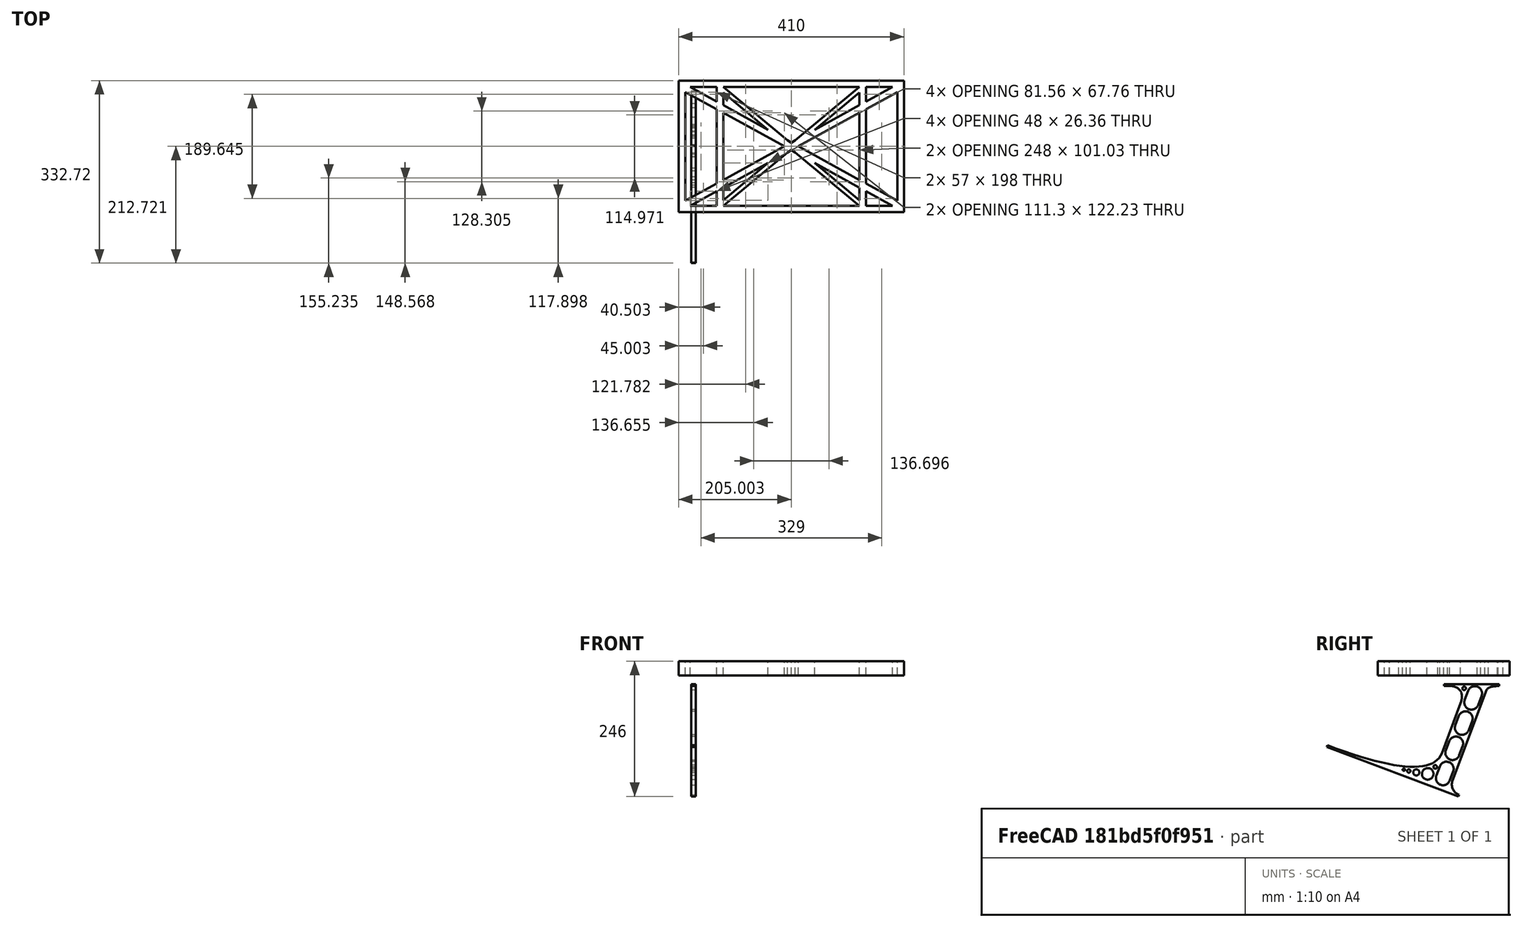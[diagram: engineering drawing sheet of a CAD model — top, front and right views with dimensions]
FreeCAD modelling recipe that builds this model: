
FCSTD DOCUMENT  (FreeCAD 0.19R0.19.2)
Label: laptopStand039
License: All rights reserved
LicenseURL: http://en.wikipedia.org/wiki/All_rights_reserved
objects: Sketcher::SketchObject×3, Part::Extrusion×2
note: 5 computed .brp shape members not serialized (recipe doc carries the construction recipe); baked Part::Feature solids carry a one-line shape summary decoded from their .brp

FEATURE [Sketcher::SketchObject] Sketch
  FullyConstrained = true
  sketch-geometry (52):
    g0: LineSegment StartX=-22.9272 StartY=136.221 StartZ=0 EndX=-22.9272 EndY=-103.779 EndZ=0
    g1: LineSegment StartX=-22.9272 StartY=136.221 StartZ=0 EndX=387.073 EndY=136.221 EndZ=0
    g2: LineSegment StartX=-22.9272 StartY=-103.779 StartZ=0 EndX=387.073 EndY=-103.779 EndZ=0
    g3: LineSegment StartX=387.073 StartY=136.221 StartZ=0 EndX=387.073 EndY=-103.779 EndZ=0
    g4: LineSegment StartX=375.073 StartY=115.221 StartZ=0 EndX=318.073 EndY=83.9235 EndZ=0
    g5: LineSegment StartX=-10.9272 StartY=-82.7794 StartZ=0 EndX=46.0728 EndY=-51.4823 EndZ=0
    g6: LineSegment StartX=-1.92719 StartY=124.221 StartZ=0 EndX=46.0728 EndY=97.8651 EndZ=0
    g7: LineSegment StartX=366.073 StartY=-91.7794 StartZ=0 EndX=318.073 EndY=-65.424 EndZ=0
    g8: LineSegment StartX=-10.9272 StartY=115.221 StartZ=0 EndX=-10.9272 EndY=-82.7794 EndZ=0
    g9: LineSegment StartX=375.073 StartY=-82.7794 StartZ=0 EndX=375.073 EndY=115.221 EndZ=0
    g10: LineSegment StartX=-1.92719 StartY=-91.7794 StartZ=0 EndX=46.0728 EndY=-91.7794 EndZ=0
    g11: LineSegment StartX=318.073 StartY=124.221 StartZ=0 EndX=366.073 EndY=124.221 EndZ=0
    g12: LineSegment StartX=306.073 StartY=-81.8102 StartZ=0 EndX=224.513 EndY=-14.0532 EndZ=0
    g13: LineSegment StartX=58.0728 StartY=114.251 StartZ=0 EndX=139.632 EndY=46.4944 EndZ=0
    g14: LineSegment StartX=306.073 StartY=124.221 StartZ=0 EndX=189.124 EndY=27.0628 EndZ=0
    g15: LineSegment StartX=58.0728 StartY=-91.7794 StartZ=0 EndX=175.022 EndY=5.37834 EndZ=0
    g16: LineSegment StartX=46.0728 StartY=124.221 StartZ=0 EndX=46.0728 EndY=97.8651 EndZ=0
    g17: LineSegment StartX=58.0728 StartY=-81.8102 StartZ=0 EndX=58.0728 EndY=-58.8351 EndZ=0
    g18: LineSegment StartX=318.073 StartY=124.221 StartZ=0 EndX=318.073 EndY=97.8651 EndZ=0
    g19: LineSegment StartX=306.073 StartY=114.251 StartZ=0 EndX=306.073 EndY=91.2763 EndZ=0
    g20: LineSegment StartX=182.073 StartY=23.1914 StartZ=0 EndX=189.124 EndY=27.0628 EndZ=0
    g21: LineSegment StartX=182.073 StartY=9.24976 StartZ=0 EndX=175.022 EndY=5.37834 EndZ=0
    g22: LineSegment StartX=224.513 StartY=46.4944 StartZ=0 EndX=306.073 EndY=114.251 EndZ=0
    g23: LineSegment StartX=175.022 StartY=27.0628 StartZ=0 EndX=58.0728 EndY=124.221 EndZ=0
    g24: LineSegment StartX=169.377 StartY=16.2206 StartZ=0 EndX=58.0728 EndY=77.3346 EndZ=0
    g25: LineSegment StartX=139.632 StartY=-14.0532 StartZ=0 EndX=58.0728 EndY=-81.8102 EndZ=0
    g26: LineSegment StartX=194.768 StartY=16.2206 StartZ=0 EndX=306.073 EndY=-44.8935 EndZ=0
    g27: LineSegment StartX=224.513 StartY=46.4944 StartZ=0 EndX=306.073 EndY=91.2763 EndZ=0
    g28: LineSegment StartX=175.022 StartY=27.0628 StartZ=0 EndX=182.073 EndY=23.1914 EndZ=0
    g29: LineSegment StartX=139.632 StartY=-14.0532 StartZ=0 EndX=58.0728 EndY=-58.8351 EndZ=0
    g30: LineSegment StartX=189.124 StartY=5.37834 StartZ=0 EndX=182.073 EndY=9.24976 EndZ=0
    g31: LineSegment StartX=189.124 StartY=5.37834 StartZ=0 EndX=306.073 EndY=-91.7794 EndZ=0
    g32: LineSegment StartX=306.073 StartY=77.3346 StartZ=0 EndX=306.073 EndY=-44.8935 EndZ=0
    g33: LineSegment StartX=318.073 StartY=83.9235 StartZ=0 EndX=318.073 EndY=-51.4823 EndZ=0
    g34: LineSegment StartX=318.073 StartY=97.8651 StartZ=0 EndX=366.073 EndY=124.221 EndZ=0
    g35: LineSegment StartX=306.073 StartY=77.3346 StartZ=0 EndX=194.768 EndY=16.2206 EndZ=0
    g36: LineSegment StartX=306.073 StartY=-58.8351 StartZ=0 EndX=224.513 EndY=-14.0532 EndZ=0
    g37: LineSegment StartX=306.073 StartY=-58.8351 StartZ=0 EndX=306.073 EndY=-81.8102 EndZ=0
    g38: LineSegment StartX=318.073 StartY=-51.4823 StartZ=0 EndX=375.073 EndY=-82.7794 EndZ=0
    g39: LineSegment StartX=318.073 StartY=-65.424 StartZ=0 EndX=318.073 EndY=-91.7794 EndZ=0
    g40: LineSegment StartX=306.073 StartY=124.221 StartZ=0 EndX=58.0728 EndY=124.221 EndZ=0
    g41: LineSegment StartX=318.073 StartY=-91.7794 StartZ=0 EndX=366.073 EndY=-91.7794 EndZ=0
    g42: LineSegment StartX=58.0728 StartY=-91.7794 StartZ=0 EndX=306.073 EndY=-91.7794 EndZ=0
    g43: LineSegment StartX=58.0728 StartY=-44.8935 StartZ=0 EndX=58.0728 EndY=77.3346 EndZ=0
    g44: LineSegment StartX=46.0728 StartY=-65.424 StartZ=0 EndX=-1.92719 EndY=-91.7794 EndZ=0
    g45: LineSegment StartX=46.0728 StartY=-65.424 StartZ=0 EndX=46.0728 EndY=-91.7794 EndZ=0
    g46: LineSegment StartX=58.0728 StartY=-44.8935 StartZ=0 EndX=169.377 EndY=16.2206 EndZ=0
    g47: LineSegment StartX=58.0728 StartY=91.2763 StartZ=0 EndX=58.0728 EndY=114.251 EndZ=0
    g48: LineSegment StartX=46.0728 StartY=83.9235 StartZ=0 EndX=46.0728 EndY=-51.4823 EndZ=0
    g49: LineSegment StartX=46.0728 StartY=124.221 StartZ=0 EndX=-1.92719 EndY=124.221 EndZ=0
    g50: LineSegment StartX=58.0728 StartY=91.2763 StartZ=0 EndX=139.632 EndY=46.4944 EndZ=0
    g51: LineSegment StartX=46.0728 StartY=83.9235 StartZ=0 EndX=-10.9272 EndY=115.221 EndZ=0
  constraints (102):
    c: Vertical(g0)
    c: Distance(g0) = 240
    c: Horizontal(g1)
    c: Distance(g1) = 410
    c: Coincident(g1,g0)
    c: Coincident(g2,g0)
    c: Horizontal(g2)
    c: Coincident(g3,g1)
    c: Vertical(g3)
    c: Coincident(g2,g3)
    c: Block(g1)
    c: Horizontal(g10)
    c: Horizontal(g11)
    c: PointOnObject(g35,g6)
    c: Coincident(g28,g20)
    c: Coincident(g30,g21)
    c: Tangent(g7,g24)
    c: PointOnObject(g24,g5)
    c: PointOnObject(g26,g4)
    c: Coincident(g20,g14)
    c: Tangent(g20,g27)
    c: Coincident(g50,g13)
    c: Coincident(g28,g23)
    c: Coincident(g22,g27)
    c: Coincident(g21,g15)
    c: Coincident(g29,g25)
    c: Tangent(g21,g29)
    c: Coincident(g36,g12)
    c: Coincident(g31,g30)
    c: Coincident(g22,g19)
    c: Tangent(g19,g32)
    c: Tangent(g18,g33)
    c: Coincident(g27,g19)
    c: Tangent(g27,g34)
    c: Coincident(g4,g33)
    c: Coincident(g35,g32)
    c: Tangent(g4,g35)
    c: Coincident(g37,g12)
    c: Tangent(g7,g36)
    c: Tangent(g32,g37)
    c: Coincident(g26,g32)
    c: Tangent(g26,g38)
    c: Coincident(g33,g38)
    c: Coincident(g39,g7)
    c: Tangent(g33,g39)
    c: Coincident(g25,g17)
    c: Tangent(g17,g43)
    c: Coincident(g29,g17)
    c: Tangent(g29,g44)
    c: Coincident(g45,g44)
    c: Tangent(g16,g45)
    c: Coincident(g5,g48)
    c: Coincident(g46,g43)
    c: Tangent(g5,g46)
    c: Tangent(g43,g47)
    c: Tangent(g16,g48)
    c: Coincident(g13,g47)
    c: PointOnObject(g40,g23)
    c: Tangent(g40,g49)
    c: Coincident(g6,g16)
    c: Coincident(g50,g47)
    c: Tangent(g6,g50)
    c: Coincident(g24,g43)
    c: Coincident(g51,g48)
    c: Tangent(g24,g51)
    c: Block(g23)
    c: Block(g14)
    c: Block(g20)
    c: Block(g40)
    c: Block(g18)
    c: Block(g34)
    c: Block(g4)
    c: Block(g38)
    c: Block(g9)
    c: Block(g36)
    c: Block(g37)
    c: Block(g7)
    c: Block(g39)
    c: Block(g22)
    c: Block(g31)
    c: Block(g42)
    c: Block(g21)
    c: Block(g15)
    c: Block(g29)
    c: Block(g25)
    c: Block(g45)
    c: Block(g44)
    c: Block(g5)
    c: Block(g8)
    c: Block(g51)
    c: Block(g6)
    c: Block(g16)
    c: Block(g13)
    c: Block(g47)
    c: Block(g35)
    c: Block(g32)
    c: Block(g24)
    c: Block(g46)
    c: Block(g49)
    c: Block(g11)
    c: Block(g41)
    c: Block(g10)
FEATURE [Part::Extrusion] Extrude
  Base = -> Sketch
  Dir = (0,0,1)
  DirMode = 2
  FaceMakerClass = Part::FaceMakerBullseye
  LengthFwd = 26
  LengthRev = 0
  Solid = true
  Symmetric = false
FEATURE [Sketcher::SketchObject] Sketch001
  FullyConstrained = true
  MapMode = 4
  Placement = pos=(0,0,0) rot=(0.57735,0.57735,0.57735;2.0944rad)
  Support = -> [Sketch]
  sketch-geometry (46):
    g0: BSplineCurve PolesCount=3 KnotsCount=2 Degree=2 IsPeriodic=0
    g1: ArcOfCircle CenterX=73.122 CenterY=-32.2909 CenterZ=0 NormalX=0 NormalY=0 NormalZ=1 AngleXU=0 Radius=13 StartAngle=5.92268 EndAngle=9.06428
    g2: ArcOfCircle CenterX=66.7816 CenterY=-49.1439 CenterZ=0 NormalX=0 NormalY=0 NormalZ=1 AngleXU=0 Radius=13 StartAngle=2.78068 EndAngle=5.92131
    g3: ArcOfCircle CenterX=55.9263 CenterY=-78.1807 CenterZ=0 NormalX=0 NormalY=0 NormalZ=1 AngleXU=0 Radius=13 StartAngle=5.92268 EndAngle=9.06428
    g4: ArcOfCircle CenterX=49.5884 CenterY=-95.0342 CenterZ=0 NormalX=0 NormalY=0 NormalZ=1 AngleXU=0 Radius=13 StartAngle=2.78068 EndAngle=5.92131
    g5: ArcOfCircle CenterX=38.7206 CenterY=-124.067 CenterZ=0 NormalX=0 NormalY=0 NormalZ=1 AngleXU=0 Radius=13 StartAngle=5.92268 EndAngle=9.06428
    g6: ArcOfCircle CenterX=32.3875 CenterY=-140.92 CenterZ=0 NormalX=0 NormalY=0 NormalZ=1 AngleXU=0 Radius=13 StartAngle=2.78068 EndAngle=5.92131
    g7: ArcOfCircle CenterX=21.4715 CenterY=-169.934 CenterZ=0 NormalX=0 NormalY=0 NormalZ=1 AngleXU=0 Radius=13 StartAngle=5.92268 EndAngle=9.06428
    g8: ArcOfCircle CenterX=15.1336 CenterY=-186.787 CenterZ=0 NormalX=0 NormalY=0 NormalZ=1 AngleXU=0 Radius=13 StartAngle=2.78068 EndAngle=5.92131
    g9-g12: Circle x4 (B-spline internal-alignment scaffolding for g13; pole/knot coordinates omitted)
    g13: BSplineCurve PolesCount=4 KnotsCount=2 Degree=3 IsPeriodic=0
    g14: GeomPoint X=28.8094 Y=-19.0875 Z=0
    g15: GeomPoint X=47.0443 Y=-50.4712 Z=0
    g16: Circle CenterX=53.5586 CenterY=-23.2695 CenterZ=0 NormalX=0 NormalY=0 NormalZ=1 AngleXU=0 Radius=3.24518
    g17: Circle CenterX=-195.441 CenterY=-127.082 CenterZ=0 NormalX=0 NormalY=0 NormalZ=1 AngleXU=0 Radius=1
    g18: Circle CenterX=-8.24091 CenterY=-197.481 CenterZ=0 NormalX=0 NormalY=0 NormalZ=1 AngleXU=0 Radius=1
    g19: Circle CenterX=12.8789 CenterY=-141.321 CenterZ=0 NormalX=0 NormalY=0 NormalZ=1 AngleXU=0 Radius=1
    g20: BSplineCurve PolesCount=3 KnotsCount=2 Degree=2 IsPeriodic=0
    g21: GeomPoint X=-195.441 Y=-127.082 Z=0
    g22: GeomPoint X=12.8789 Y=-141.321 Z=0
    g23: Circle CenterX=-12.8016 CenterY=-179.036 CenterZ=0 NormalX=0 NormalY=0 NormalZ=1 AngleXU=0 Radius=10.5072
    g24: Circle CenterX=0.933922 CenterY=-166.43 CenterZ=0 NormalX=0 NormalY=0 NormalZ=1 AngleXU=0 Radius=3.26661
    g25: Circle CenterX=-33.5518 CenterY=-176.44 CenterZ=0 NormalX=0 NormalY=0 NormalZ=1 AngleXU=0 Radius=5.64388
    g26: Circle CenterX=-47.2366 CenterY=-173.859 CenterZ=0 NormalX=0 NormalY=0 NormalZ=1 AngleXU=0 Radius=3.01653
    g27: Circle CenterX=-56.2595 CenterY=-171.456 CenterZ=0 NormalX=0 NormalY=0 NormalZ=1 AngleXU=0 Radius=2.12826
    g28: ArcOfCircle CenterX=51.2151 CenterY=-198.473 CenterZ=0 NormalX=0 NormalY=0 NormalZ=1 AngleXU=0 Radius=20 StartAngle=2.78189 EndAngle=4.35269
    g29: LineSegment StartX=32.4951 StartY=-191.433 StartZ=0 EndX=94.6577 EndY=-26.1351 EndZ=0
    g30: LineSegment StartX=43.1192 StartY=-220.001 StartZ=0 EndX=-196.497 EndY=-129.89 EndZ=0
    g31: LineSegment StartX=43.1192 StartY=-220.001 StartZ=0 EndX=44.1752 EndY=-217.193 EndZ=0
    g32: LineSegment StartX=117.223 StartY=-19.0875 StartZ=0 EndX=117.223 EndY=-16.0875 EndZ=0
    g33: LineSegment StartX=117.223 StartY=-16.0875 StartZ=0 EndX=17.2232 EndY=-16.0875 EndZ=0
    g34: LineSegment StartX=17.2232 StartY=-16.0875 StartZ=0 EndX=17.2232 EndY=-19.0875 EndZ=0
    g35: LineSegment StartX=28.8094 StartY=-19.0875 StartZ=0 EndX=17.2232 EndY=-19.0875 EndZ=0
    g36: LineSegment StartX=47.0443 StartY=-50.4712 StartZ=0 EndX=12.8789 EndY=-141.321 EndZ=0
    g37: LineSegment StartX=-195.441 StartY=-127.082 StartZ=0 EndX=-196.497 EndY=-129.89 EndZ=0
    g38: LineSegment StartX=85.2864 StartY=-36.8765 StartZ=0 EndX=78.9396 EndY=-53.7463 EndZ=0
    g39: LineSegment StartX=60.9577 StartY=-27.7052 StartZ=0 EndX=54.6191 EndY=-44.5532 EndZ=0
    g40: LineSegment StartX=68.0907 StartY=-82.7664 StartZ=0 EndX=61.7465 EndY=-99.6365 EndZ=0
    g41: LineSegment StartX=43.7619 StartY=-73.595 StartZ=0 EndX=37.426 EndY=-90.4435 EndZ=0
    g42: LineSegment StartX=50.885 StartY=-128.652 StartZ=0 EndX=44.5456 EndY=-145.522 EndZ=0
    g43: LineSegment StartX=26.5562 StartY=-119.481 StartZ=0 EndX=20.2251 EndY=-136.329 EndZ=0
    g44: LineSegment StartX=9.3071 StartY=-165.349 StartZ=0 EndX=2.97115 EndY=-182.197 EndZ=0
    g45: LineSegment StartX=33.6358 StartY=-174.52 StartZ=0 EndX=27.2917 EndY=-191.39 EndZ=0
  constraints (70):
    c: Block(g0)
    c: Block(g1)
    c: Block(g2)
    c: Block(g4)
    c: Block(g3)
    c: Block(g6)
    c: Block(g5)
    c: Block(g8)
    c: Block(g7)
    c: Weight(g9) = 1
    c: Equal(g9,g10)
    c: Equal(g9,g11)
    c: Equal(g9,g12)
    c: InternalAlignment(g9-g12 -> g13) x4
    c: InternalAlignment(g14,g13)
    c: InternalAlignment(g15,g13)
    c: Block(g16)
    c: Weight(g17) = 1
    c: Equal(g17,g18)
    c: Equal(g17,g19)
    c: InternalAlignment(g17,g20)
    c: InternalAlignment(g18,g20)
    c: InternalAlignment(g19,g20)
    c: InternalAlignment(g21,g20)
    c: InternalAlignment(g22,g20)
    c: Block(g20)
    c: Block(g23)
    c: Block(g24)
    c: Block(g25)
    c: Block(g26)
    c: Block(g27)
    c: Block(g28)
    c: Coincident(g29,g28)
    c: Coincident(g29,g0)
    c: Block(g13)
    c: Coincident(g31,g30)
    c: Coincident(g31,g28)
    c: Block(g31)
    c: Coincident(g32,g0)
    c: Vertical(g32)
    c: Coincident(g33,g32)
    c: Horizontal(g33)
    c: Coincident(g34,g33)
    c: Vertical(g34)
    c: Block(g33)
    c: Coincident(g35,g13)
    c: Coincident(g35,g34)
    c: Horizontal(g35)
    c: Coincident(g36,g13)
    c: Coincident(g36,g20)
    c: Coincident(g37,g20)
    c: Coincident(g37,g30)
    c: Block(g30)
    c: Coincident(g38,g1)
    c: Coincident(g38,g2)
    c: Coincident(g39,g1)
    c: Coincident(g39,g2)
    c: Coincident(g40,g3)
    c: Coincident(g40,g4)
    c: Coincident(g41,g3)
    c: Coincident(g41,g4)
    c: Coincident(g42,g5)
    c: Coincident(g42,g6)
    c: Coincident(g43,g5)
    c: Coincident(g43,g6)
    c: Coincident(g44,g7)
    c: Coincident(g44,g8)
    c: Coincident(g45,g7)
    c: Coincident(g45,g8)
    c: Distance(g30) = 256
FEATURE [Part::Extrusion] Extrude002
  Base = -> Sketch001
  Dir = (1,0,0)
  DirMode = 2
  FaceMakerClass = Part::FaceMakerBullseye
  LengthFwd = 8
  LengthRev = 0
  Solid = true
  Symmetric = false
FEATURE [Sketcher::SketchObject] Sketch002
  FullyConstrained = true
  sketch-geometry (20):
    g0: LineSegment StartX=-2.77179 StartY=-200.304 StartZ=0 EndX=5.22821 EndY=-200.304 EndZ=0
    g1: LineSegment StartX=5.22821 StartY=-200.304 StartZ=0 EndX=5.22821 EndY=-197.304 EndZ=0
    g2: LineSegment StartX=-2.77179 StartY=-200.304 StartZ=0 EndX=-2.77179 EndY=-197.304 EndZ=0
    g3: LineSegment StartX=5.22821 StartY=-197.304 StartZ=0 EndX=8.22821 EndY=-197.304 EndZ=0
    g4: LineSegment StartX=-2.77179 StartY=-197.304 StartZ=0 EndX=-5.77179 EndY=-197.304 EndZ=0
    g5: LineSegment StartX=19.2282 StartY=-203.304 StartZ=0 EndX=19.2282 EndY=-206.304 EndZ=0
    g6: LineSegment StartX=-16.7718 StartY=-203.304 StartZ=0 EndX=-16.7718 EndY=-206.304 EndZ=0
    g7: LineSegment StartX=-16.7718 StartY=-206.304 StartZ=0 EndX=19.2282 EndY=-206.304 EndZ=0
    g8: Circle CenterX=-16.7718 CenterY=-203.304 CenterZ=0 NormalX=0 NormalY=0 NormalZ=1 AngleXU=0 Radius=1
    g9: Circle CenterX=-5.77179 CenterY=-203.304 CenterZ=0 NormalX=0 NormalY=0 NormalZ=1 AngleXU=0 Radius=1
    g10: Circle CenterX=-5.77179 CenterY=-197.304 CenterZ=0 NormalX=0 NormalY=0 NormalZ=1 AngleXU=0 Radius=1
    g11: BSplineCurve PolesCount=3 KnotsCount=2 Degree=2 IsPeriodic=0
    g12: GeomPoint X=-16.7718 Y=-203.304 Z=0
    g13: GeomPoint X=-5.77179 Y=-197.304 Z=0
    g14: Circle CenterX=19.2282 CenterY=-203.304 CenterZ=0 NormalX=0 NormalY=0 NormalZ=1 AngleXU=0 Radius=1
    g15: Circle CenterX=8.22821 CenterY=-203.304 CenterZ=0 NormalX=0 NormalY=0 NormalZ=1 AngleXU=0 Radius=1
    g16: Circle CenterX=8.22821 CenterY=-197.304 CenterZ=0 NormalX=0 NormalY=0 NormalZ=1 AngleXU=0 Radius=1
    g17: BSplineCurve PolesCount=3 KnotsCount=2 Degree=2 IsPeriodic=0
    g18: GeomPoint X=19.2282 Y=-203.304 Z=0
    g19: GeomPoint X=8.22821 Y=-197.304 Z=0
  constraints (41):
    c: Horizontal(g0)
    c: Distance(g0) = 8
    c: Coincident(g1,g0)
    c: Vertical(g1)
    c: Distance(g1) = 3
    c: Coincident(g2,g0)
    c: Vertical(g2)
    c: Distance(g2) = 3
    c: Coincident(g3,g1)
    c: Horizontal(g3)
    c: Distance(g3) = 3
    c: Coincident(g4,g2)
    c: Horizontal(g4)
    c: Distance(g4) = 3
    c: Vertical(g5)
    c: Vertical(g6)
    c: Coincident(g7,g6)
    c: Coincident(g7,g5)
    c: Weight(g8) = 1
    c: Equal(g8,g9)
    c: Equal(g8,g10)
    c: Coincident(g11,g4)
    c: InternalAlignment(g8,g11)
    c: InternalAlignment(g9,g11)
    c: InternalAlignment(g10,g11)
    c: InternalAlignment(g12,g11)
    c: InternalAlignment(g13,g11)
    c: Coincident(g17,g5)
    c: Weight(g14) = 1
    c: Equal(g14,g15)
    c: Equal(g14,g16)
    c: Coincident(g17,g3)
    c: InternalAlignment(g14,g17)
    c: InternalAlignment(g15,g17)
    c: InternalAlignment(g16,g17)
    c: InternalAlignment(g18,g17)
    c: InternalAlignment(g19,g17)
    c: Block(g7)
    c: Block(g17)
    c: Block(g11)
    c: Block(g6)
